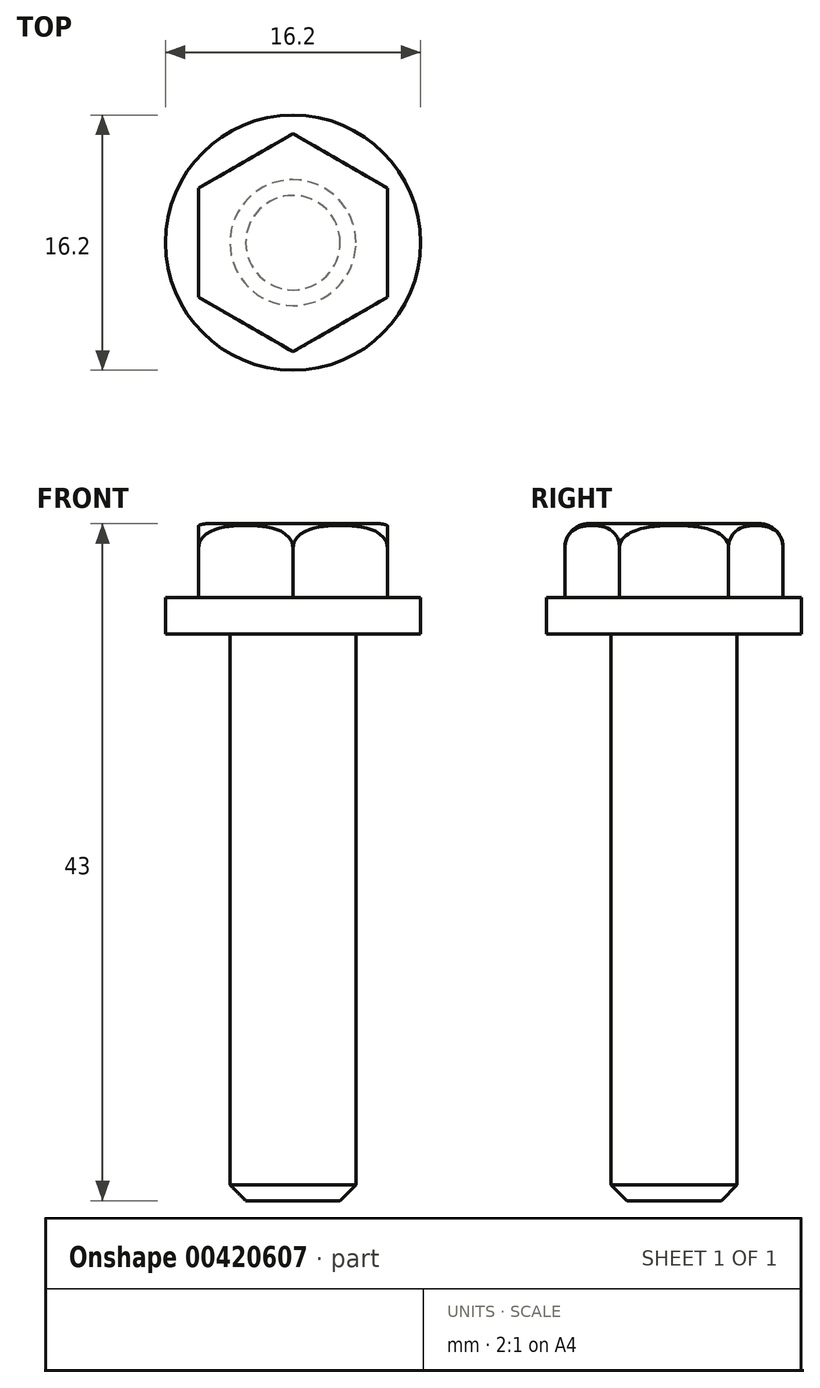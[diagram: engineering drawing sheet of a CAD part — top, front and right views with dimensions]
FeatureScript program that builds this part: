
annotation { "Feature Type Name" : "Feature", "Feature Type Description" : "" }
export const myFeature = defineFeature(function(context is Context, id is Id, definition is map)
    precondition{}
    {
        {
            var Q0;
            Q0=qCreatedBy(makeId("Front.planeOp"),FACE);
            var sketch = newSketch(context, id + "F0", { "sketchPlane" : qUnion([Q0])});
            skLineSegment(sketch, "E0", {"start": v(0, 0) * mm, "end": v(0, 48.7) * mm, "construction": true});
            skLineSegment(sketch, "E1", {"start": v(0, 0) * mm, "end": v(-4, 0) * mm});
            skLineSegment(sketch, "E2", {"start": v(-4, 0) * mm, "end": v(-4, 36) * mm});
            skLineSegment(sketch, "E3", {"start": v(-4, 36) * mm, "end": v(-6.93, 36) * mm});
            skLineSegment(sketch, "E4", {"start": v(-6.93, 36) * mm, "end": v(-6.93, 43) * mm});
            skLineSegment(sketch, "E5", {"start": v(-6.93, 43) * mm, "end": v(0, 43) * mm});
            skLineSegment(sketch, "E6", {"start": v(0, 43) * mm, "end": v(0, 0) * mm});
            skCircle(sketch, "E7.cCircle", {"center": v(0, 43) * mm, "radius": 6 * mm, "construction": true});
            skLineSegment(sketch, "E7.0", {"start": v(-6.93, 43) * mm, "end": v(-3.46, 49) * mm, "construction": true});
            skLineSegment(sketch, "E7.1", {"start": v(-3.46, 49) * mm, "end": v(3.46, 49) * mm, "construction": true});
            skLineSegment(sketch, "E7.2", {"start": v(3.46, 49) * mm, "end": v(6.93, 43) * mm, "construction": true});
            skLineSegment(sketch, "E7.3", {"start": v(6.93, 43) * mm, "end": v(3.46, 37) * mm, "construction": true});
            skLineSegment(sketch, "E7.4", {"start": v(3.46, 37) * mm, "end": v(-3.46, 37) * mm, "construction": true});
            skLineSegment(sketch, "E7.5", {"start": v(-3.46, 37) * mm, "end": v(-6.93, 43) * mm, "construction": true});
            skPoint(sketch, "E7.0.midPoint", {"position": v(-5.2, 46) * mm});
            skSolve(sketch);
        }
        {
            var Q0;
            Q0=makeQuery(id+"F0.imprint","IMPRINT",FACE,{"disambiguationData":[TD([[makeQuery(id+"F0.imprint","IMPRINT",EDGE,{"derivedFrom":sQuery(id+"F0.wireOp",EDGE,"E1")}),-1.0]])]});
            var Q1;
            Q1=sQuery(id+"F0.wireOp",EDGE,"E0");
            revolve(context, id + "F1", {"entities" : qUnion([Q0]), "axis" : qUnion([Q1]), "revolveType" : RevolveType.FULL});
        }
        {
            var Q0;
            Q0=makeQuery(id+"F1.opRevolve","SWEPT_EDGE",EDGE,{"disambiguationData":[OSD([sQuery(id+"F0.wireOp",EDGE,"E4"),sQuery(id+"F0.wireOp",EDGE,"E5")])]});
            fillet(context, id + "F2", {"entities" : qUnion([Q0]), "radius" : 1.5 * mm, "tangentPropagation" : true, "allowEdgeOverflow" : false});
        }
        {
            var Q0;
            Q0=makeQuery(id+"F1.opRevolve","SWEPT_FACE",FACE,{"disambiguationData":[OSD([sQuery(id+"F0.wireOp",EDGE,"E5")])]});
            var sketch = newSketch(context, id + "F3", { "sketchPlane" : qUnion([Q0])});
            skCircle(sketch, "E8.cCircle", {"center": v(0, 0) * mm, "radius": 6 * mm, "construction": true});
            skLineSegment(sketch, "E8.0", {"start": v(-6, -3.46) * mm, "end": v(-6, 3.46) * mm});
            skLineSegment(sketch, "E8.1", {"start": v(-6, 3.46) * mm, "end": v(0, 6.93) * mm});
            skLineSegment(sketch, "E8.2", {"start": v(0, 6.93) * mm, "end": v(6, 3.46) * mm});
            skLineSegment(sketch, "E8.3", {"start": v(6, 3.46) * mm, "end": v(6, -3.46) * mm});
            skLineSegment(sketch, "E8.4", {"start": v(6, -3.46) * mm, "end": v(0, -6.93) * mm});
            skLineSegment(sketch, "E8.5", {"start": v(0, -6.93) * mm, "end": v(-6, -3.46) * mm});
            skPoint(sketch, "E8.0.midPoint", {"position": v(-6, 0) * mm});
            skCircle(sketch, "E9", {"center": v(0, 0) * mm, "radius": 8 * mm});
            skSolve(sketch);
        }
        {
            var Q0;
            Q0 = qSketchRegion(id + "F3", true);
            extrude(context, id + "F4", {"entities" : qUnion([Q0]), "operationType" : NewBodyOperationType.REMOVE, "endBound" : BoundingType.THROUGH_ALL, "oppositeDirection" : true, "depth" : 25 * mm, "offsetDistance" : 25 * mm});
        }
        {
            var Q0;
            Q0=qCreatedBy(makeId("Front.planeOp"),FACE);
            var sketch = newSketch(context, id + "F5", { "sketchPlane" : qUnion([Q0])});
            skLineSegment(sketch, "E10", {"start": v(0, 36) * mm, "end": v(-8.1, 36) * mm});
            skLineSegment(sketch, "E11", {"start": v(-8.1, 36) * mm, "end": v(-8.1, 38.3) * mm});
            skLineSegment(sketch, "E12", {"start": v(0, 38.3) * mm, "end": v(0, 36) * mm});
            skLineSegment(sketch, "E13", {"start": v(0, 36) * mm, "end": v(0, 23.9) * mm, "construction": true});
            skLineSegment(sketch, "E14", {"start": v(-8.1, 38.3) * mm, "end": v(0, 38.3) * mm});
            skSolve(sketch);
        }
        {
            var Q0;
            Q0 = qSketchRegion(id + "F5", true);
            var Q1;
            Q1=sQuery(id+"F5.wireOp",EDGE,"E13");
            revolve(context, id + "F6", {"operationType" : NewBodyOperationType.ADD, "entities" : qUnion([Q0]), "axis" : qUnion([Q1]), "revolveType" : RevolveType.FULL});
        }
        {
            var Q0;
            Q0=makeQuery(id+"F1.opRevolve","SWEPT_EDGE",EDGE,{"disambiguationData":[OSD([sQuery(id+"F0.wireOp",EDGE,"E1"),sQuery(id+"F0.wireOp",EDGE,"E2")])]});
            chamfer(context, id + "F7", {"entities" : qUnion([Q0]), "width" : 1 * mm, "tangentPropagation" : true});
        }
    });
